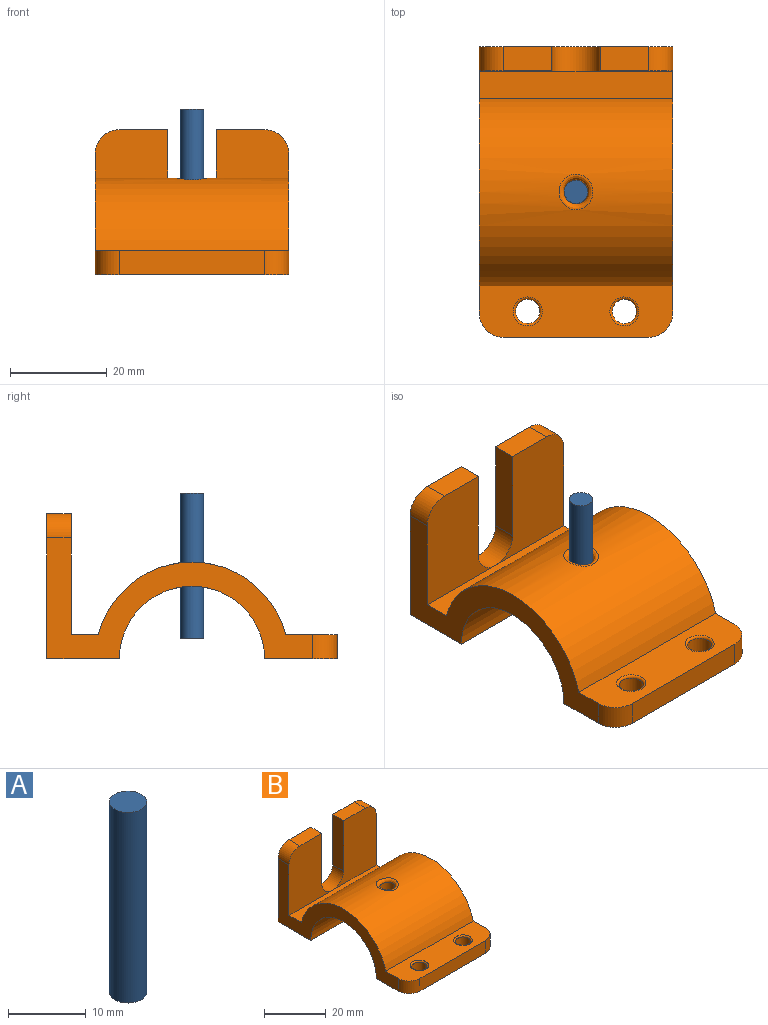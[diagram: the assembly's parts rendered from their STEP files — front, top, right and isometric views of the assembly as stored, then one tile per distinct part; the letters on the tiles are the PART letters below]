
ASSEMBLY  parts=2 mates=1
PART A: 3 faces, bbox 4.8x4.8x30 mm
  f0: cylinder r=2.4mm len=30mm, axis (0,0,-1), area 452.4mm2, adj f1,f2
  f1: plane 4.8x4.8mm, normal (0,0,1), area 18.1mm2, adj f0
  f2: plane 4.8x4.8mm, normal (0,0,-1), area 18.1mm2, adj f0
PART B: 30 faces, bbox 40x60x30 mm
  f0: cylinder r=20mm len=40mm, axis (-1,0,0), area 2068.2mm2, adj f5,f6,f12,f13,f24
  f1: cylinder r=15mm len=40mm, axis (-1,0,0), area 1848.7mm2, adj f8,f9,f12,f13,f25
  f2: plane 10x5mm, normal (0,0,1), area 50mm2, adj f3,f10,f14,f17
  f3: plane 25x20mm, normal (0,-1,0), area 375mm2, adj f2,f5,f12,f14,f16,f17
  f4: plane 25x20mm, normal (0,-1,0), area 375mm2, adj f5,f11,f13,f15,f16,f18
  f5: plane 40x5.64mm, normal (0,0,1), area 225.4mm2, adj f0,f3,f4,f12,f13
  f6: plane 40x10.64mm, normal (0,0,1), area 358.1mm2, adj f0,f7,f12,f13,f19,f20,f28,f29
  f7: plane 30x5mm, normal (0,-1,0), area 150mm2, adj f6,f8,f19,f20
  f8: plane 40x15mm, normal (0,0,-1), area 532.7mm2, adj f1,f7,f12,f13,f19,f20,f26,f27
  f9: plane 40x15mm, normal (0,0,-1), area 600mm2, adj f1,f10,f12,f13
  f10: plane 40x30mm, normal (0,1,0), area 950mm2, adj f2,f9,f11,f12,f13,f14,f15,f16
  f11: plane 10x5mm, normal (0,0,1), area 50mm2, adj f4,f10,f15,f18
  f12: plane 55x25mm, normal (1,0,0), area 452mm2, adj f0,f1,f3,f5,f6,f8,f9,f10
  f13: plane 55x25mm, normal (-1,0,0), area 452mm2, adj f0,f1,f4,f5,f6,f8,f9,f10
  f14: plane 20x5mm, normal (-1,0,0), area 100mm2, adj f2,f3,f10,f16
  f15: plane 20x5mm, normal (1,0,0), area 100mm2, adj f4,f10,f11,f16
  f16: cylinder r=5mm len=10mm, axis (0,1,0), area 78.5mm2, adj f3,f4,f10,f14,f15
  f17: cylinder r=5mm len=5mm, axis (0,1,0), area 39.3mm2, adj f2,f3,f10,f12
  f18: cylinder r=5mm len=5mm, axis (0,-1,0), area 39.3mm2, adj f4,f10,f11,f13
  f19: cylinder r=5mm len=5mm, axis (0,0,1), area 39.3mm2, adj f6,f7,f8,f12
  f20: cylinder r=5mm len=5mm, axis (0,0,-1), area 39.3mm2, adj f6,f7,f8,f13
  f21: cylinder r=2.5mm len=5mm, axis (0,0,1), area 62.8mm2, adj f27,f28
  f22: cylinder r=2.5mm len=5mm, axis (0,0,1), area 62.8mm2, adj f26,f29
  f23: cylinder r=2.5mm len=5mm, axis (0,0,-1), area 47.6mm2, adj f24,f25
  f24: bspline ~7.37x7.01mm, area 30.4mm2, adj f0,f23
  f25: bspline ~7x6.57mm, area 25.9mm2, adj f1,f23
  f26: torus R=3mm, axis (0,0,1), area 13.2mm2, adj f8,f22
  f27: torus R=3mm, axis (0,0,1), area 13.2mm2, adj f8,f21
  f28: torus R=3mm, axis (0,0,1), area 13.2mm2, adj f6,f21
  f29: torus R=3mm, axis (0,0,1), area 13.2mm2, adj f6,f22
PLACE A t=(41.79,-8.25,5.73)mm
PLACE B t=(10.63,-8.25,1.49)mm
MATE slider B.f23 <-> A.f0  axis (0,0,-1) through (30.63,-8.25,20.52)mm
